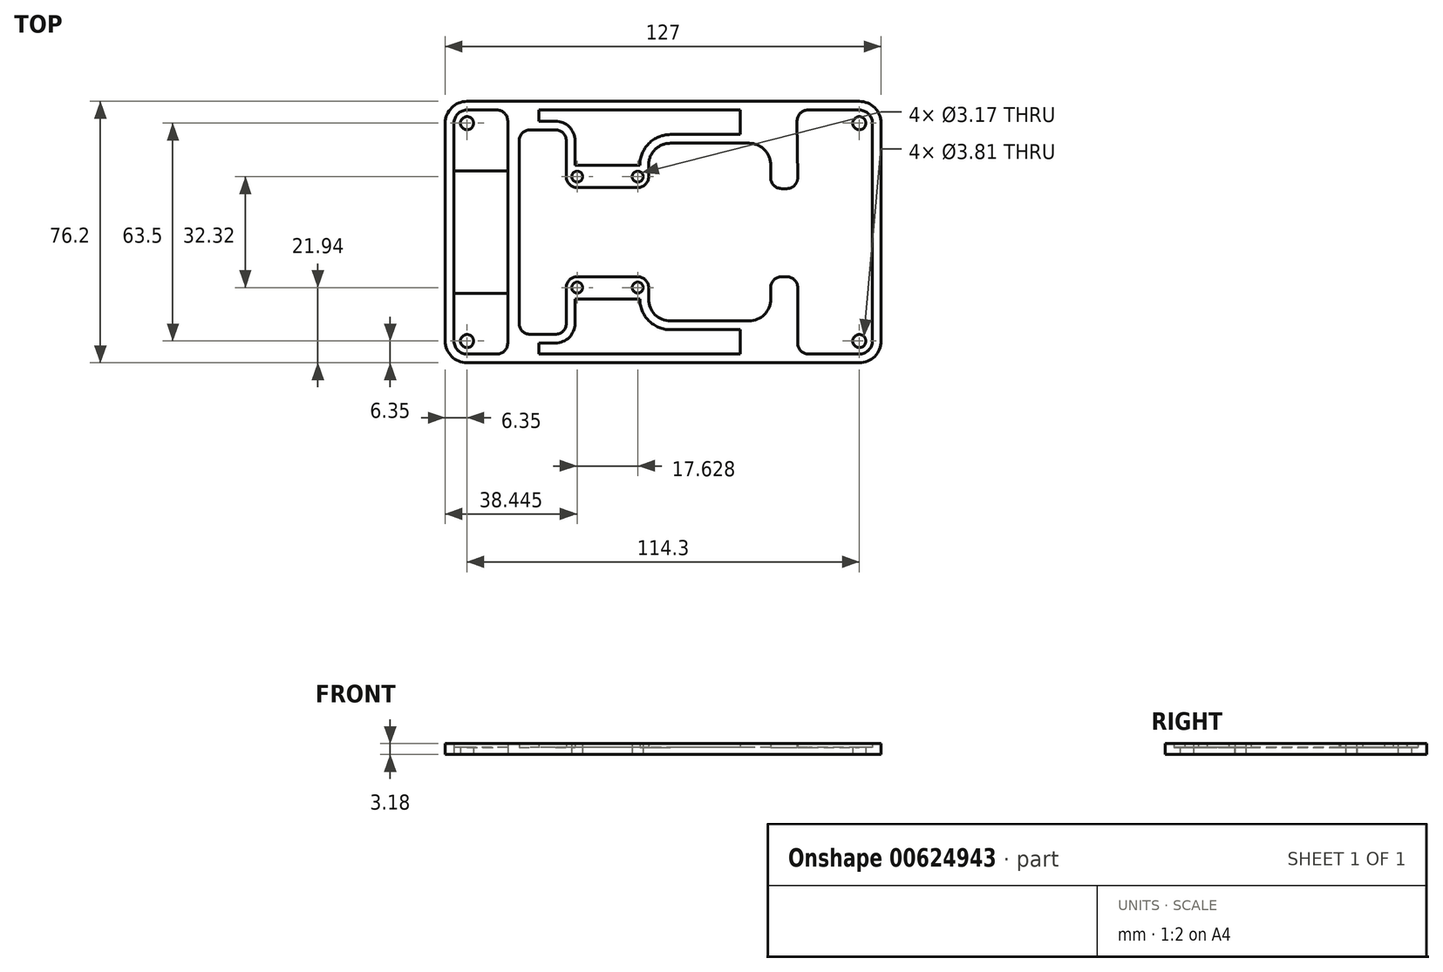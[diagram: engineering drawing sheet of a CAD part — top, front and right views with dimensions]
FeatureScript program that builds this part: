
annotation { "Feature Type Name" : "Feature", "Feature Type Description" : "" }
export const myFeature = defineFeature(function(context is Context, id is Id, definition is map)
    precondition{}
    {
        {
            var Q0;
            Q0=qCreatedBy(makeId("Top.planeOp"),FACE);
            var sketch = newSketch(context, id + "F0", { "sketchPlane" : qUnion([Q0])});
            skLineSegment(sketch, "E0.bottom", {"start": v(6.35, 0) * mm, "end": v(120.65, 0) * mm});
            skLineSegment(sketch, "E0.top", {"start": v(6.35, 76.2) * mm, "end": v(120.65, 76.2) * mm});
            skLineSegment(sketch, "E0.left", {"start": v(0, 6.35) * mm, "end": v(0, 69.85) * mm});
            skLineSegment(sketch, "E0.right", {"start": v(127, 6.35) * mm, "end": v(127, 69.85) * mm});
            skPoint(sketch, "E1.visualSharp", {"position": v(0, 76.2) * mm});
            skArc(sketch, "E1.filletArc", {"start": v(6.35, 76.2) * mm, "mid": v(1.86, 74.34) * mm, "end": v(0, 69.85) * mm});
            skPoint(sketch, "E2.visualSharp", {"position": v(127, 76.2) * mm});
            skArc(sketch, "E2.filletArc", {"start": v(127, 69.85) * mm, "mid": v(125.14, 74.34) * mm, "end": v(120.65, 76.2) * mm});
            skPoint(sketch, "E3.visualSharp", {"position": v(127, 0) * mm});
            skArc(sketch, "E3.filletArc", {"start": v(120.65, 0) * mm, "mid": v(125.14, 1.86) * mm, "end": v(127, 6.35) * mm});
            skArc(sketch, "E4.filletArc", {"start": v(0, 6.35) * mm, "mid": v(1.86, 1.86) * mm, "end": v(6.35, 0) * mm});
            skLineSegment(sketch, "E5.0", {"start": v(2.54, 6.35) * mm, "end": v(2.54, 69.85) * mm});
            skArc(sketch, "E5.1", {"start": v(6.35, 73.66) * mm, "mid": v(3.66, 72.54) * mm, "end": v(2.54, 69.85) * mm});
            skArc(sketch, "E5.2", {"start": v(2.54, 6.35) * mm, "mid": v(3.66, 3.66) * mm, "end": v(6.35, 2.54) * mm});
            skLineSegment(sketch, "E5.3", {"start": v(6.35, 73.66) * mm, "end": v(15.05, 73.66) * mm});
            skLineSegment(sketch, "E5.4", {"start": v(6.35, 2.54) * mm, "end": v(15.05, 2.54) * mm});
            skArc(sketch, "E5.5", {"start": v(120.65, 2.54) * mm, "mid": v(123.34, 3.66) * mm, "end": v(124.46, 6.35) * mm});
            skLineSegment(sketch, "E5.6", {"start": v(124.46, 6.35) * mm, "end": v(124.46, 69.85) * mm});
            skArc(sketch, "E5.7", {"start": v(124.46, 69.85) * mm, "mid": v(123.34, 72.54) * mm, "end": v(120.65, 73.66) * mm});
            skLineSegment(sketch, "E6.left", {"start": v(18.22, 70.49) * mm, "end": v(18.22, 5.71) * mm});
            skLineSegment(sketch, "E7.bottom", {"start": v(88.5, 64) * mm, "end": v(65.6, 64) * mm});
            skLineSegment(sketch, "E7.top", {"start": v(88.5, 12.2) * mm, "end": v(65.6, 12.2) * mm});
            skPoint(sketch, "E8.visualSharp", {"position": v(59.25, 64) * mm});
            skArc(sketch, "E8.filletArc", {"start": v(65.6, 64) * mm, "mid": v(61.1, 62.13) * mm, "end": v(59.25, 57.64) * mm});
            skPoint(sketch, "E9.visualSharp", {"position": v(94.84, 64) * mm});
            skArc(sketch, "E9.filletArc", {"start": v(94.84, 57.64) * mm, "mid": v(92.98, 62.14) * mm, "end": v(88.5, 64) * mm});
            skPoint(sketch, "E10.visualSharp", {"position": v(94.84, 12.2) * mm});
            skArc(sketch, "E10.filletArc", {"start": v(88.5, 12.2) * mm, "mid": v(92.98, 14.06) * mm, "end": v(94.84, 18.55) * mm});
            skPoint(sketch, "E11.visualSharp", {"position": v(59.25, 12.2) * mm});
            skArc(sketch, "E11.filletArc", {"start": v(59.25, 18.55) * mm, "mid": v(61.1, 14.06) * mm, "end": v(65.6, 12.2) * mm});
            skPoint(sketch, "E12.centerSnap0", {"position": v(38.56, 38.1) * mm});
            skLineSegment(sketch, "E13.bottom", {"start": v(32.1, 67.9) * mm, "end": v(24.69, 67.9) * mm});
            skLineSegment(sketch, "E13.top", {"start": v(32.1, 8.3) * mm, "end": v(24.69, 8.3) * mm});
            skLineSegment(sketch, "E13.right", {"start": v(21.51, 64.72) * mm, "end": v(21.51, 11.48) * mm});
            skPoint(sketch, "E14.visualSharp", {"position": v(21.51, 67.9) * mm});
            skArc(sketch, "E14.filletArc", {"start": v(24.69, 67.9) * mm, "mid": v(22.44, 66.97) * mm, "end": v(21.51, 64.72) * mm});
            skPoint(sketch, "E15.visualSharp", {"position": v(35.27, 67.9) * mm});
            skArc(sketch, "E15.filletArc", {"start": v(35.27, 64.72) * mm, "mid": v(34.34, 66.97) * mm, "end": v(32.1, 67.9) * mm});
            skPoint(sketch, "E16.visualSharp", {"position": v(35.27, 8.3) * mm});
            skArc(sketch, "E16.filletArc", {"start": v(32.1, 8.3) * mm, "mid": v(34.34, 9.23) * mm, "end": v(35.27, 11.48) * mm});
            skPoint(sketch, "E17.visualSharp", {"position": v(21.51, 8.3) * mm});
            skArc(sketch, "E17.filletArc", {"start": v(21.51, 11.48) * mm, "mid": v(22.44, 9.23) * mm, "end": v(24.69, 8.3) * mm});
            skPoint(sketch, "E18.middle", {"position": v(77.05, 38.1) * mm});
            skLineSegment(sketch, "E19", {"start": v(120.65, 2.54) * mm, "end": v(105.87, 2.54) * mm});
            skLineSegment(sketch, "E20", {"start": v(105.7, 73.66) * mm, "end": v(120.65, 73.66) * mm});
            skPoint(sketch, "E21.visualSharp", {"position": v(105.5, 73.66) * mm});
            skArc(sketch, "E21.filletArc", {"start": v(105.7, 73.66) * mm, "mid": v(103.48, 72.76) * mm, "end": v(102.52, 70.57) * mm});
            skPoint(sketch, "E22.visualSharp", {"position": v(102.27, 2.54) * mm});
            skArc(sketch, "E22.filletArc", {"start": v(102.7, 5.71) * mm, "mid": v(103.63, 3.47) * mm, "end": v(105.87, 2.54) * mm});
            skPoint(sketch, "E23.visualSharp", {"position": v(18.22, 2.54) * mm});
            skArc(sketch, "E23.filletArc", {"start": v(15.05, 2.54) * mm, "mid": v(17.3, 3.47) * mm, "end": v(18.22, 5.71) * mm});
            skPoint(sketch, "E24.visualSharp", {"position": v(18.22, 73.66) * mm});
            skArc(sketch, "E24.filletArc", {"start": v(18.22, 70.49) * mm, "mid": v(17.3, 72.73) * mm, "end": v(15.05, 73.66) * mm});
            skPoint(sketch, "E25.middle.positionSnap0", {"position": v(63.5, 76.2) * mm});
            skPoint(sketch, "E25.centerSnap0", {"position": v(63.5, 76.2) * mm});
            skLineSegment(sketch, "E26", {"start": v(35.27, 64.72) * mm, "end": v(35.27, 54.26) * mm});
            skLineSegment(sketch, "E27", {"start": v(35.27, 11.48) * mm, "end": v(35.27, 21.94) * mm});
            skLineSegment(sketch, "E28", {"start": v(59.25, 57.64) * mm, "end": v(59.25, 54.26) * mm});
            skLineSegment(sketch, "E29", {"start": v(59.25, 18.55) * mm, "end": v(59.25, 21.94) * mm});
            skLineSegment(sketch, "E30", {"start": v(94.84, 57.64) * mm, "end": v(94.84, 53.95) * mm});
            skLineSegment(sketch, "E31", {"start": v(102.7, 53.98) * mm, "end": v(102.52, 70.57) * mm});
            skLineSegment(sketch, "E32", {"start": v(102.7, 21.94) * mm, "end": v(102.7, 5.71) * mm});
            skLineSegment(sketch, "E33", {"start": v(38.45, 51.08) * mm, "end": v(56.07, 51.08) * mm});
            skLineSegment(sketch, "E34", {"start": v(98.02, 50.77) * mm, "end": v(99.52, 50.77) * mm});
            skLineSegment(sketch, "E35", {"start": v(56.07, 25.12) * mm, "end": v(38.45, 25.12) * mm});
            skLineSegment(sketch, "E36", {"start": v(99.52, 25.11) * mm, "end": v(98.02, 25.11) * mm});
            skLineSegment(sketch, "E37", {"start": v(94.84, 21.94) * mm, "end": v(94.84, 18.55) * mm});
            skPoint(sketch, "E38.visualSharp", {"position": v(35.27, 51.08) * mm});
            skArc(sketch, "E38.filletArc", {"start": v(35.27, 54.26) * mm, "mid": v(36.2, 52.01) * mm, "end": v(38.45, 51.08) * mm});
            skPoint(sketch, "E39.visualSharp", {"position": v(59.25, 51.08) * mm});
            skArc(sketch, "E39.filletArc", {"start": v(56.07, 51.08) * mm, "mid": v(58.32, 52.01) * mm, "end": v(59.25, 54.26) * mm});
            skPoint(sketch, "E40.visualSharp", {"position": v(59.25, 25.12) * mm});
            skArc(sketch, "E40.filletArc", {"start": v(59.25, 21.94) * mm, "mid": v(58.32, 24.19) * mm, "end": v(56.07, 25.12) * mm});
            skPoint(sketch, "E41.visualSharp", {"position": v(35.27, 25.12) * mm});
            skArc(sketch, "E41.filletArc", {"start": v(38.45, 25.12) * mm, "mid": v(36.2, 24.19) * mm, "end": v(35.27, 21.94) * mm});
            skPoint(sketch, "E42.visualSharp", {"position": v(102.73, 50.77) * mm});
            skArc(sketch, "E42.filletArc", {"start": v(99.52, 50.77) * mm, "mid": v(101.78, 51.71) * mm, "end": v(102.7, 53.98) * mm});
            skArc(sketch, "E43.filletArc", {"start": v(102.7, 21.94) * mm, "mid": v(101.76, 24.18) * mm, "end": v(99.52, 25.11) * mm});
            skPoint(sketch, "E44.visualSharp", {"position": v(94.84, 50.77) * mm});
            skArc(sketch, "E44.filletArc", {"start": v(94.84, 53.95) * mm, "mid": v(95.77, 51.7) * mm, "end": v(98.02, 50.77) * mm});
            skArc(sketch, "E45.filletArc", {"start": v(98.02, 25.11) * mm, "mid": v(95.77, 24.18) * mm, "end": v(94.84, 21.94) * mm});
            skCircle(sketch, "E46", {"center": v(38.45, 54.26) * mm, "radius": 1.59 * mm});
            skCircle(sketch, "E47", {"center": v(56.07, 54.26) * mm, "radius": 1.59 * mm});
            skCircle(sketch, "E48", {"center": v(38.45, 21.94) * mm, "radius": 1.59 * mm});
            skCircle(sketch, "E49", {"center": v(56.07, 21.94) * mm, "radius": 1.59 * mm});
            skLineSegment(sketch, "E50", {"start": v(24.69, 67.9) * mm, "end": v(24.69, 76.2) * mm});
            skLineSegment(sketch, "E51", {"start": v(88.5, 64) * mm, "end": v(88.5, 76.2) * mm});
            skLineSegment(sketch, "E52", {"start": v(88.5, 76.2) * mm, "end": v(24.69, 76.2) * mm});
            skLineSegment(sketch, "E53.1", {"start": v(85.95, 73.66) * mm, "end": v(27.23, 73.66) * mm});
            skLineSegment(sketch, "E53.2", {"start": v(85.95, 66.54) * mm, "end": v(85.95, 73.66) * mm});
            skLineSegment(sketch, "E53.3", {"start": v(85.95, 66.54) * mm, "end": v(65.6, 66.54) * mm});
            skArc(sketch, "E54.0", {"start": v(65.6, 66.54) * mm, "mid": v(59.3, 63.93) * mm, "end": v(56.7, 57.63) * mm});
            skArc(sketch, "E55.0", {"start": v(37.81, 64.72) * mm, "mid": v(36.14, 68.76) * mm, "end": v(32.1, 70.44) * mm});
            skLineSegment(sketch, "E56", {"start": v(32.1, 70.44) * mm, "end": v(27.23, 70.44) * mm});
            skLineSegment(sketch, "E57", {"start": v(27.23, 70.44) * mm, "end": v(27.23, 73.66) * mm});
            skLineSegment(sketch, "E58", {"start": v(56.7, 57.63) * mm, "end": v(37.81, 57.63) * mm});
            skLineSegment(sketch, "E59", {"start": v(37.81, 57.63) * mm, "end": v(37.81, 64.72) * mm});
            skLineSegment(sketch, "E60.MirrorCS", {"start": v(56.7, 18.57) * mm, "end": v(37.81, 18.57) * mm});
            skArc(sketch, "E61.MirrorCS", {"start": v(65.6, 9.66) * mm, "mid": v(59.3, 12.27) * mm, "end": v(56.7, 18.57) * mm});
            skLineSegment(sketch, "E62.MirrorCS", {"start": v(85.95, 9.66) * mm, "end": v(65.6, 9.66) * mm});
            skLineSegment(sketch, "E63.MirrorCS", {"start": v(85.95, 9.66) * mm, "end": v(85.95, 2.54) * mm});
            skLineSegment(sketch, "E64.MirrorCS", {"start": v(85.95, 2.54) * mm, "end": v(27.23, 2.54) * mm});
            skLineSegment(sketch, "E65.MirrorCS", {"start": v(27.23, 5.76) * mm, "end": v(27.23, 2.54) * mm});
            skLineSegment(sketch, "E66.MirrorCS", {"start": v(32.1, 5.76) * mm, "end": v(27.23, 5.76) * mm});
            skArc(sketch, "E67.MirrorCS", {"start": v(37.81, 11.48) * mm, "mid": v(36.14, 7.44) * mm, "end": v(32.1, 5.76) * mm});
            skLineSegment(sketch, "E68.MirrorCS", {"start": v(37.81, 18.57) * mm, "end": v(37.81, 11.48) * mm});
            skLineSegment(sketch, "E69", {"start": v(2.54, 55.92) * mm, "end": v(18.22, 55.92) * mm});
            skLineSegment(sketch, "E70", {"start": v(102.67, 55.92) * mm, "end": v(124.46, 55.92) * mm});
            skLineSegment(sketch, "E71", {"start": v(18.22, 20.28) * mm, "end": v(2.54, 20.28) * mm});
            skLineSegment(sketch, "E72", {"start": v(102.7, 20.28) * mm, "end": v(124.46, 20.26) * mm});
            skCircle(sketch, "E73", {"center": v(6.35, 6.35) * mm, "radius": 1.9 * mm});
            skCircle(sketch, "E74", {"center": v(6.35, 69.85) * mm, "radius": 1.9 * mm});
            skCircle(sketch, "E75", {"center": v(120.65, 69.85) * mm, "radius": 1.9 * mm});
            skCircle(sketch, "E76", {"center": v(120.65, 6.35) * mm, "radius": 1.9 * mm});
            skSolve(sketch);
        }
        {
            var Q0;
            Q0=makeQuery(id+"F0.imprint","IMPRINT",FACE,{"disambiguationData":[TD([[makeQuery(id+"F0.imprint","IMPRINT",EDGE,{"derivedFrom":sQuery(id+"F0.wireOp",EDGE,"E0.bottom")}),1.0]])]});
            extrude(context, id + "F1", {"entities" : qUnion([Q0]), "depth" : 3.17 * mm, "offsetDistance" : 25.4 * mm});
        }
        {
            var Q0;
            Q0=makeQuery(id+"F0.imprint","IMPRINT",FACE,{"disambiguationData":[TD([[makeQuery(id+"F0.imprint","IMPRINT",EDGE,{"derivedFrom":sQuery(id+"F0.wireOp",EDGE,"E7.bottom")}),-1.0]])]});
            extrude(context, id + "F2", {"entities" : qUnion([Q0]), "operationType" : NewBodyOperationType.ADD, "depth" : 3.17 * mm, "offsetDistance" : 25.4 * mm});
        }
        {
            var Q0;
            Q0=makeQuery(id+"F0.imprint","IMPRINT",FACE,{"disambiguationData":[TD([[makeQuery(id+"F0.imprint","IMPRINT",EDGE,{"derivedFrom":sQuery(id+"F0.wireOp",EDGE,"E53.1")}),1.0]])]});
            extrude(context, id + "F3", {"entities" : qUnion([Q0]), "operationType" : NewBodyOperationType.ADD, "depth" : 2.03 * mm, "offsetDistance" : 25.4 * mm});
        }
        {
            var Q0;
            Q0=makeQuery(id+"F0.imprint","IMPRINT",FACE,{"disambiguationData":[TD([[makeQuery(id+"F0.imprint","IMPRINT",EDGE,{"derivedFrom":sQuery(id+"F0.wireOp",EDGE,"E7.bottom")}),1.0]])]});
            extrude(context, id + "F4", {"entities" : qUnion([Q0]), "operationType" : NewBodyOperationType.ADD, "depth" : 2.03 * mm, "offsetDistance" : 25.4 * mm});
        }
        {
            var Q0;
            Q0=makeQuery(id+"F0.imprint","IMPRINT",FACE,{"disambiguationData":[TD([[makeQuery(id+"F0.imprint","IMPRINT",EDGE,{"derivedFrom":sQuery(id+"F0.wireOp",EDGE,"E60.MirrorCS")}),1.0]])]});
            extrude(context, id + "F5", {"entities" : qUnion([Q0]), "operationType" : NewBodyOperationType.ADD, "depth" : 2.03 * mm, "offsetDistance" : 25.4 * mm});
        }
        {
            var Q0;
            {var subQ3=sQuery(id+"F0.wireOp",EDGE,"E5.2");Q0=makeQuery(id+"F0.imprint","IMPRINT",FACE,{"disambiguationData":[TD([[makeQuery(id+"F0.imprint","IMPRINT",EDGE,{"derivedFrom":subQ3}),1.0]])]});}
            extrude(context, id + "F6", {"entities" : qUnion([Q0]), "operationType" : NewBodyOperationType.ADD, "depth" : 2.03 * mm, "offsetDistance" : 25.4 * mm});
        }
        {
            var Q0;
            {var subQ3=sQuery(id+"F0.wireOp",EDGE,"E5.7");Q0=makeQuery(id+"F0.imprint","IMPRINT",FACE,{"disambiguationData":[TD([[makeQuery(id+"F0.imprint","IMPRINT",EDGE,{"derivedFrom":subQ3}),1.0]])]});}
            var Q1;
            {var subQ3=sQuery(id+"F0.wireOp",EDGE,"E5.1");Q1=makeQuery(id+"F0.imprint","IMPRINT",FACE,{"disambiguationData":[TD([[makeQuery(id+"F0.imprint","IMPRINT",EDGE,{"derivedFrom":subQ3}),1.0]])]});}
            var Q2;
            {var subQ1=sQuery(id+"F0.wireOp",EDGE,"E5.5");Q2=makeQuery(id+"F0.imprint","IMPRINT",FACE,{"disambiguationData":[TD([[makeQuery(id+"F0.imprint","IMPRINT",EDGE,{"derivedFrom":subQ1}),1.0]])]});}
            extrude(context, id + "F7", {"entities" : qUnion([Q0, Q1, Q2]), "operationType" : NewBodyOperationType.ADD, "depth" : 2.03 * mm, "offsetDistance" : 25.4 * mm});
        }
    });
